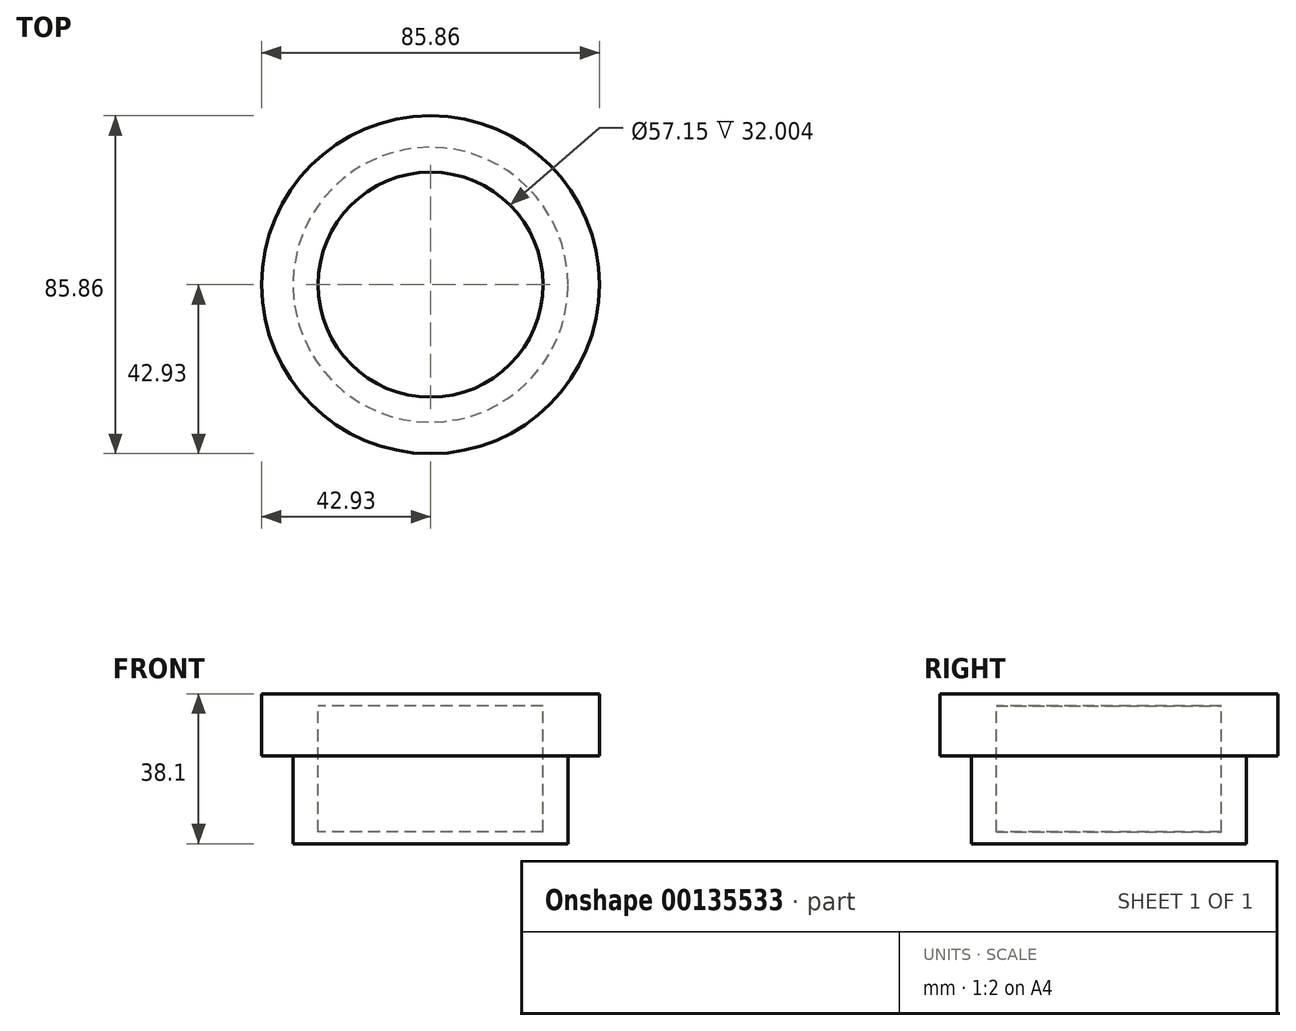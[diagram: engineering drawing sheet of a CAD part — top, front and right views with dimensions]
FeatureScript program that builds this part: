
annotation { "Feature Type Name" : "Feature", "Feature Type Description" : "" }
export const myFeature = defineFeature(function(context is Context, id is Id, definition is map)
    precondition{}
    {
        {
            var Q0;
            Q0=qCreatedBy(makeId("Front.planeOp"),FACE);
            var sketch = newSketch(context, id + "F0", { "sketchPlane" : qUnion([Q0])});
            skLineSegment(sketch, "E0", {"start": v(0, 0) * mm, "end": v(0, -38.1) * mm});
            skLineSegment(sketch, "E1", {"start": v(0, -38.1) * mm, "end": v(34.93, -38.1) * mm});
            skLineSegment(sketch, "E2", {"start": v(0, -35.05) * mm, "end": v(28.58, -35.05) * mm});
            skLineSegment(sketch, "E3", {"start": v(28.58, 0) * mm, "end": v(0, 0) * mm});
            skLineSegment(sketch, "E4", {"start": v(28.58, -35.05) * mm, "end": v(28.58, -3.05) * mm});
            skLineSegment(sketch, "E5", {"start": v(28.58, -3.05) * mm, "end": v(0, -3.05) * mm});
            skLineSegment(sketch, "E6", {"start": v(28.58, 0) * mm, "end": v(28.58, -15.75) * mm});
            skLineSegment(sketch, "E7", {"start": v(34.93, -38.1) * mm, "end": v(34.93, -15.75) * mm});
            skLineSegment(sketch, "E8", {"start": v(0, 0) * mm, "end": v(42.93, 0) * mm});
            skLineSegment(sketch, "E9", {"start": v(42.93, 0) * mm, "end": v(42.93, -15.75) * mm});
            skLineSegment(sketch, "E10", {"start": v(42.93, -15.75) * mm, "end": v(34.93, -15.75) * mm});
            skLineSegment(sketch, "E11", {"start": v(0, -41.36) * mm, "end": v(0, 14.16) * mm, "construction": true});
            skPoint(sketch, "E11.endSnap0", {"position": v(0, -19.05) * mm});
            skLineSegment(sketch, "E12", {"start": v(42.93, 0) * mm, "end": v(28.58, 0) * mm});
            skLineSegment(sketch, "E13", {"start": v(28.58, -35.05) * mm, "end": v(34.93, -35.05) * mm});
            skPoint(sketch, "E13.endSnap0", {"position": v(34.93, -26.92) * mm});
            skSolve(sketch);
        }
        {
            var Q0;
            {var subQ3=sQuery(id+"F0.wireOp",EDGE,"E5");Q0=makeQuery(id+"F0.imprint","IMPRINT",FACE,{"disambiguationData":[TD([[makeQuery(id+"F0.imprint","IMPRINT",EDGE,{"derivedFrom":subQ3}),-1.0]])]});}
            var Q1;
            {var subQ2=sQuery(id+"F0.wireOp",EDGE,"E2");Q1=makeQuery(id+"F0.imprint","IMPRINT",FACE,{"disambiguationData":[TD([[makeQuery(id+"F0.imprint","IMPRINT",EDGE,{"derivedFrom":subQ2}),1.0]])]});}
            var Q2;
            Q2=sQuery(id+"F0.wireOp",EDGE,"E10");
            var Q3;
            Q3=sQuery(id+"F0.wireOp",EDGE,"E9");
            var Q4;
            Q4=sQuery(id+"F0.wireOp",EDGE,"E4");
            var Q5;
            Q5=sQuery(id+"F0.wireOp",EDGE,"E7");
            var Q6;
            Q6=sQuery(id+"F0.wireOp",EDGE,"E12");
            var Q7;
            Q7=sQuery(id+"F0.wireOp",EDGE,"E2");
            var Q8;
            Q8=sQuery(id+"F0.wireOp",EDGE,"E11");
            revolve(context, id + "F1", {"bodyType" : ToolBodyType.SURFACE, "entities" : qUnion([Q0, Q1]), "surfaceEntities" : qUnion([Q2, Q3, Q4, Q5, Q6, Q7]), "axis" : qUnion([Q8]), "revolveType" : RevolveType.FULL});
        }
    });
